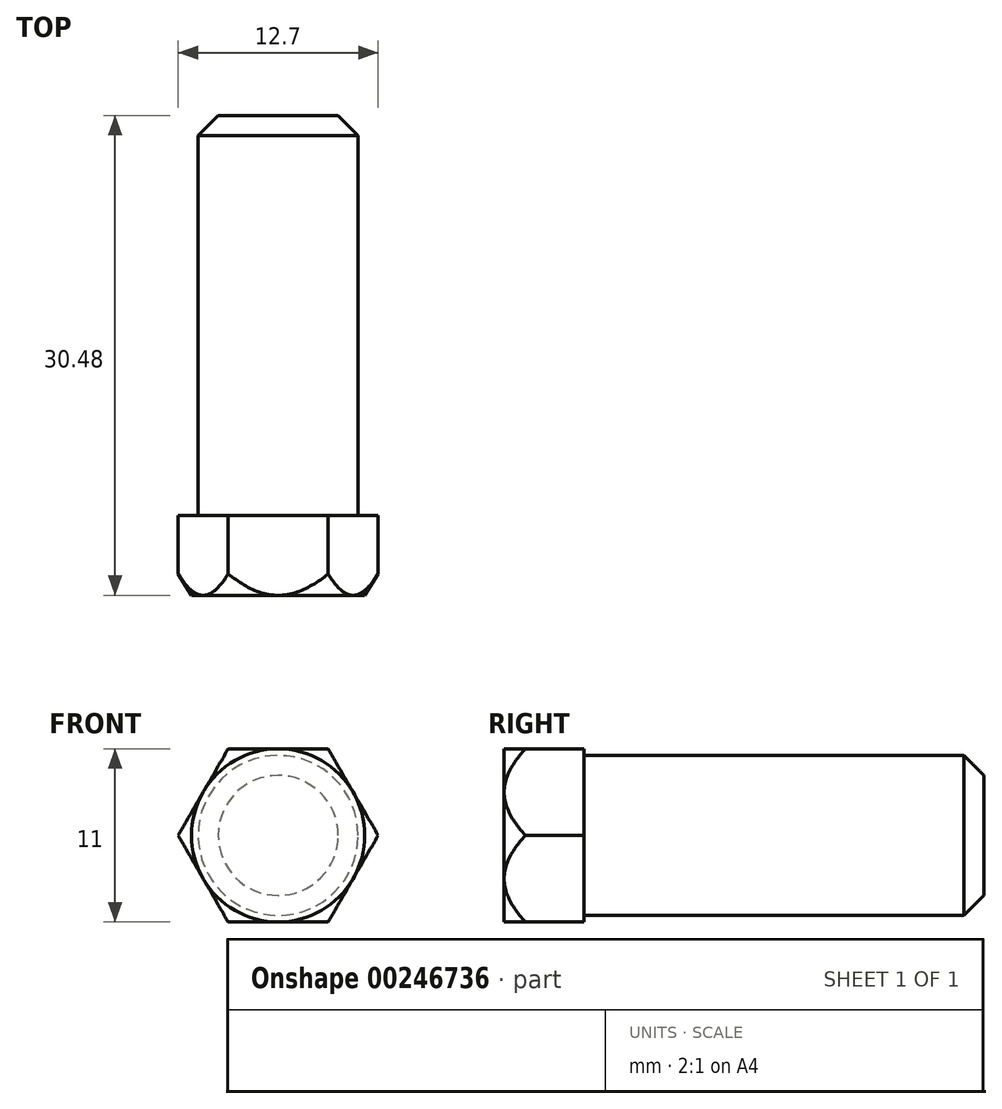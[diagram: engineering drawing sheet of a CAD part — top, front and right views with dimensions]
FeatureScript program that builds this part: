
annotation { "Feature Type Name" : "Feature", "Feature Type Description" : "" }
export const myFeature = defineFeature(function(context is Context, id is Id, definition is map)
    precondition{}
    {
        {
            var Q0;
            Q0=qCreatedBy(makeId("Front.planeOp"),FACE);
            var sketch = newSketch(context, id + "F0", { "sketchPlane" : qUnion([Q0])});
            skCircle(sketch, "E0.cCircle", {"center": v(0, 0) * mm, "radius": 6.35 * mm, "construction": true});
            skLineSegment(sketch, "E0.0", {"start": v(-6.35, 0) * mm, "end": v(-3.18, 5.5) * mm});
            skLineSegment(sketch, "E0.1", {"start": v(-3.18, 5.5) * mm, "end": v(3.17, 5.5) * mm});
            skLineSegment(sketch, "E0.2", {"start": v(3.17, 5.5) * mm, "end": v(6.35, 0) * mm});
            skLineSegment(sketch, "E0.3", {"start": v(6.35, 0) * mm, "end": v(3.18, -5.5) * mm});
            skLineSegment(sketch, "E0.4", {"start": v(3.18, -5.5) * mm, "end": v(-3.17, -5.5) * mm});
            skLineSegment(sketch, "E0.5", {"start": v(-3.17, -5.5) * mm, "end": v(-6.35, 0) * mm});
            skSolve(sketch);
        }
        {
            var Q0;
            Q0 = qSketchRegion(id + "F0", true);
            extrude(context, id + "F1", {"entities" : qUnion([Q0]), "oppositeDirection" : true, "depth" : 5.08 * mm});
        }
        {
            var Q0;
            Q0=makeQuery(id+"F1.opExtrude","CAP_FACE",FACE,{"disambiguationData":[OSD([sQuery(id+"F0.wireOp",EDGE,"E0.0"),sQuery(id+"F0.wireOp",EDGE,"E0.1"),sQuery(id+"F0.wireOp",EDGE,"E0.2"),sQuery(id+"F0.wireOp",EDGE,"E0.3"),sQuery(id+"F0.wireOp",EDGE,"E0.4"),sQuery(id+"F0.wireOp",EDGE,"E0.5")])],"isStart":true});
            var sketch = newSketch(context, id + "F2", { "sketchPlane" : qUnion([Q0])});
            skCircle(sketch, "E1", {"center": v(0, 0) * mm, "radius": 5.5 * mm});
            skCircle(sketch, "E2", {"center": v(0, 0) * mm, "radius": 8.5 * mm});
            skSolve(sketch);
        }
        {
            var Q0;
            Q0 = qSketchRegion(id + "F2", true);
            extrude(context, id + "F3", {"entities" : qUnion([Q0]), "operationType" : NewBodyOperationType.REMOVE, "oppositeDirection" : true, "depth" : 25.4 * mm, "hasDraft" : true, "draftAngle" : 32 * degree, "draftPullDirection" : true});
        }
        {
            var Q0;
            Q0=makeQuery(id+"F1.opExtrude","CAP_FACE",FACE,{"disambiguationData":[OSD([sQuery(id+"F0.wireOp",EDGE,"E0.0"),sQuery(id+"F0.wireOp",EDGE,"E0.1"),sQuery(id+"F0.wireOp",EDGE,"E0.2"),sQuery(id+"F0.wireOp",EDGE,"E0.3"),sQuery(id+"F0.wireOp",EDGE,"E0.4"),sQuery(id+"F0.wireOp",EDGE,"E0.5")])],"isStart":false});
            var sketch = newSketch(context, id + "F4", { "sketchPlane" : qUnion([Q0])});
            skCircle(sketch, "E3", {"center": v(0, 0) * mm, "radius": 5.08 * mm});
            skSolve(sketch);
        }
        {
            var Q0;
            Q0 = qSketchRegion(id + "F4", true);
            extrude(context, id + "F5", {"entities" : qUnion([Q0]), "operationType" : NewBodyOperationType.ADD, "depth" : 25.4 * mm});
        }
        {
            var Q0;
            Q0=makeQuery(id+"F5.opExtrude","CAP_EDGE",EDGE,{"disambiguationData":[OSD([sQuery(id+"F4.wireOp",EDGE,"E3")])],"isStart":false});
            chamfer(context, id + "F6", {"entities" : qUnion([Q0]), "width" : 1.27 * mm, "tangentPropagation" : true});
        }
    });
